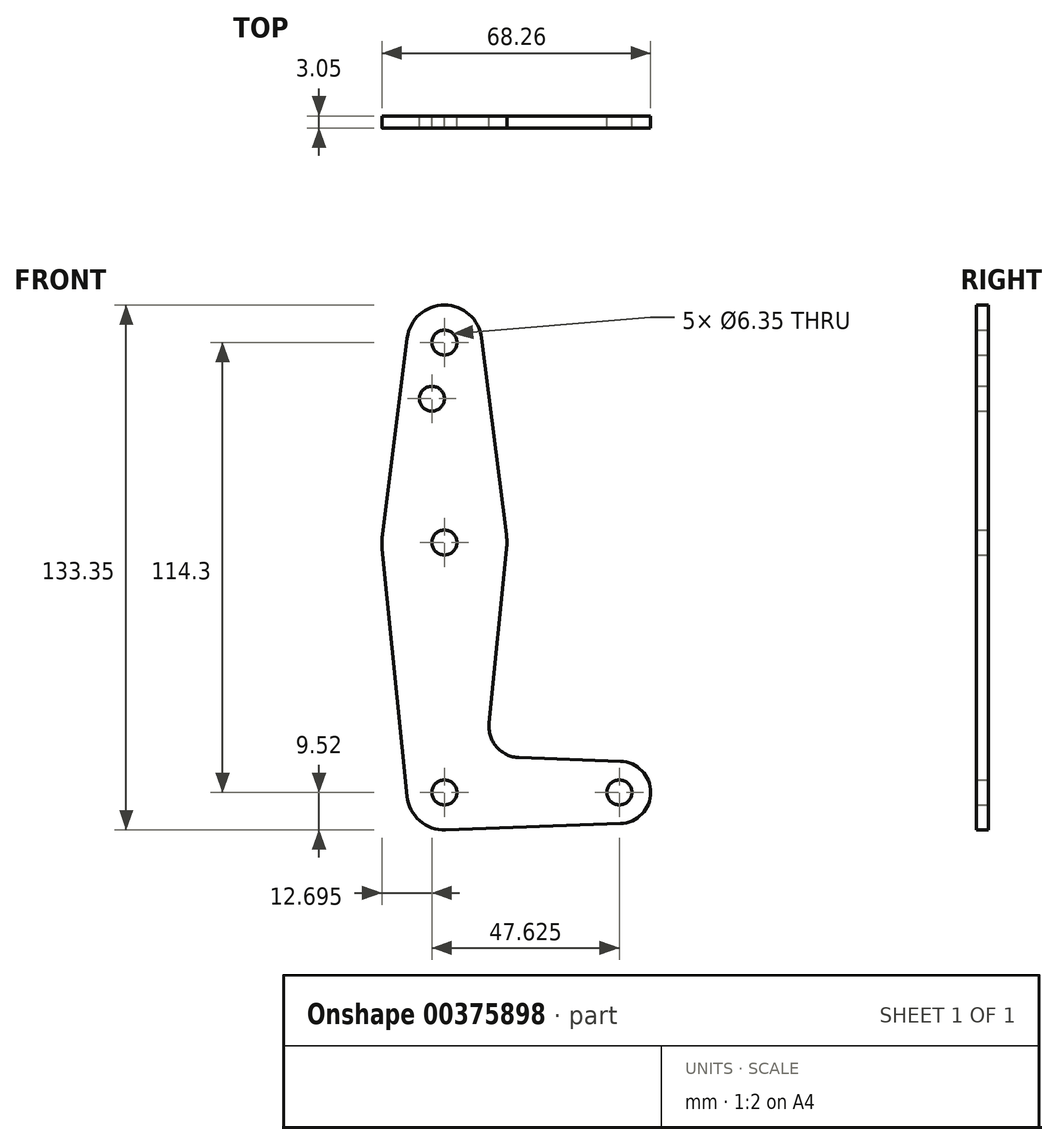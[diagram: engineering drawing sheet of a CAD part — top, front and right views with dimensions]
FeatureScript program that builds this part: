
annotation { "Feature Type Name" : "Feature", "Feature Type Description" : "" }
export const myFeature = defineFeature(function(context is Context, id is Id, definition is map)
    precondition{}
    {
        {
            var Q0;
            Q0=qCreatedBy(makeId("Front.planeOp"),FACE);
            var sketch = newSketch(context, id + "F0", { "sketchPlane" : qUnion([Q0])});
            skCircle(sketch, "E0", {"center": v(0, 0) * mm, "radius": 9.53 * mm});
            skLineSegment(sketch, "E1", {"start": v(0, 0) * mm, "end": v(44.45, 0) * mm, "construction": true});
            skLineSegment(sketch, "E2", {"start": v(0, 0) * mm, "end": v(0, 114.3) * mm, "construction": true});
            skCircle(sketch, "E3", {"center": v(0, 114.3) * mm, "radius": 9.53 * mm});
            skCircle(sketch, "E4", {"center": v(0, 63.5) * mm, "radius": 15.88 * mm});
            skCircle(sketch, "E5", {"center": v(44.45, 0) * mm, "radius": 7.94 * mm});
            skLineSegment(sketch, "E6", {"start": v(9.45, 115.5) * mm, "end": v(15.75, 65.48) * mm});
            skLineSegment(sketch, "E7", {"start": v(-9.45, 115.5) * mm, "end": v(-15.75, 65.48) * mm});
            skLineSegment(sketch, "E8", {"start": v(-15.8, 61.91) * mm, "end": v(-9.48, -0.95) * mm});
            skLineSegment(sketch, "E9", {"start": v(15.8, 61.91) * mm, "end": v(11.34, 17.6) * mm});
            skLineSegment(sketch, "E10", {"start": v(44.73, -7.93) * mm, "end": v(0, -9.53) * mm});
            skLineSegment(sketch, "E11", {"start": v(44.73, 7.93) * mm, "end": v(18.97, 8.85) * mm});
            skCircle(sketch, "E12", {"center": v(0, 114.3) * mm, "radius": 3.18 * mm});
            skCircle(sketch, "E13", {"center": v(0, 63.5) * mm, "radius": 3.18 * mm});
            skCircle(sketch, "E14", {"center": v(0, 0) * mm, "radius": 3.18 * mm});
            skCircle(sketch, "E15", {"center": v(44.45, 0) * mm, "radius": 3.18 * mm});
            skCircle(sketch, "E16", {"center": v(-3.18, 100.03) * mm, "radius": 3.18 * mm});
            skLineSegment(sketch, "E17", {"start": v(0, 100.03) * mm, "end": v(-3.18, 100.03) * mm, "construction": true});
            skLineSegment(sketch, "E18", {"start": v(-3.18, 100.03) * mm, "end": v(0, 100.03) * mm});
            skLineSegment(sketch, "E19", {"start": v(-3.18, 100.03) * mm, "end": v(-3.17, 63.5) * mm, "construction": true});
            skArc(sketch, "E20.filletArc", {"start": v(11.34, 17.6) * mm, "mid": v(13.26, 11.57) * mm, "end": v(18.97, 8.85) * mm});
            skSolve(sketch);
        }
        {
            var Q0;
            Q0 = qSketchRegion(id + "F0", true);
            extrude(context, id + "F1", {"entities" : qUnion([Q0]), "depth" : 3.05 * mm});
        }
    });
